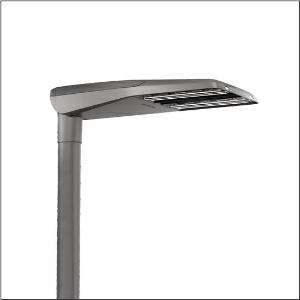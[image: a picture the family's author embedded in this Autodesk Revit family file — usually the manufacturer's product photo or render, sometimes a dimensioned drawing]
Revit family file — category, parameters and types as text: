
# Revit family: streetlight_sl_11_iq_midi___st1_2p1_0_5xc3g51e08me_ff57
name_source: partatom
category: Lighting Fixtures
units: mm (PartAtom-declared; Revit-internal decimal feet)

## family parameters
Cut with Voids When Loaded = No
Host = Face
Light Source = No
Part Type = Normal
Room Calculation Point = No
Round Connector Dimension = Use Diameter
Shared = No

## types (1)
- --- (1 x LED, 17750 lm, 124.7 W, 3000K)
    Apparent Load = 125 VA
    CIE Flux Codes = 31 68 95 100 100
    Color Rendering = 70
    Color Temperature = 3000K
    Default Elevation = 1800 mm
    Description = Streetlight SL 11 iQ midi, mast luminaire, primary light control with 3 zone facetted reflector, of plastic, silver coated, highly specular, primary optical cover: cover, of PMMA, transparent, light distribution: ST1.2P1.0, light emission: direct distribution, primary light characteristic: asymmetric, installation type: post-top, side-entry, LED, High Power LED, rated luminous flux: 17.750lm, luminous efficacy: 142lm/W, light colour: 730, colour temperature: 3000K, control: optimised constant luminous flux control (CLO 2.0), Desk-Remote (wireless, voltage-free reading and setting of iQ features in the workshop via application-optimized NFC function/RFID function), Light-Fading, Smart-Wire, Night-Set, Lumen-Switch, Temp-Guard, Auto-Match, with cable H07RN-F 5x 1.5mm², mains connection: 230..240V, AC, 50/60Hz, connection cable pre-assembled, cable length: 12,5m, start of lifetime: 125W, end of service life: 132W, reduction: 57W, luminaire housing, of diecast aluminium, powder-coated, Siteco® metallic grey (DB 702S), please order mast flange separately, inclination adjustable without tools: 0°, 5°, 10°, 15° (post-top) | 0°, -5°, -10°, -15° (side-entry), sealing non-destructively replaceable, multi-level sealing system, length: 780mm, width: 376mm, height: 118mm, mast flange for spigot size: 42mm (side-entry): 5XC10008XM4, 60/48mm (side-entry/post-top): 5XC10108XM2, 76/60mm (side-entry/post-top): 5XC10108XM1, equipment: Power, protection rating (complete): IP66, insulation class (complete): insulation class II (safety insulation), certification: CE, ENEC, VDE, impact resistance: IK09, permissible operating ambient temperature for outdoor applications: -25..+50°C, standard-compliant lighting for roads and squares, Environmental Product Declaration (EPD) tested and certified by an independent institute, packaging unit: 1 piece

Light Distribution: ST1.2P1.0
    Height = 118 mm
    Lamp = 1 x LED
    Lamp Light Flux = 17750 lm
    Lamp Power = 124.7 W
    Lamp count = 1
    Length = 780 mm
    Luminous efficacy = 142 lm/W
    Manufacturer = Siteco
    ModVariant = No
    Model = 5XC3G51E08ME
    Number of Poles = 1
    OnlyDefault = Yes
    Power Factor = 1
    Product Name = Streetlight SL 11 iQ midi | ST1.2P1.0
    Product group = mast luminaire | pylon top
    ProductGroupID = 6100
    Protection Class = Protection class II
    Protection Degree = IP 66
    RLX_Detail_Level = 1
    RLX_Emergency_Light_Flux = 0 lm
    RLX_Emergency_Type = 0
    RLX_Emergency_Type_DB = No
    RlxData = <blob elided: 70849 chars, md5=e2051bce>
    Socket = socket
    Standby Power = 0 W
    System Light Flux = 17750 lm
    System Power = 125 W
    Type Comments = factory setting: luminous flux: 100 % | dim-lin: 254 | 557 mA
    Type Image = l_1005960.jpg
    URL = http://relux.com
    VarID = @adj_129535
    Voltage = 0 V
    Weight = 0.00 kg
    Width = 376 mm

## geometry (parser evidence)
native form markers: Blend x4, Sweep x8
no freeform markers — native parametric forms only
